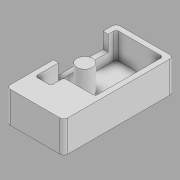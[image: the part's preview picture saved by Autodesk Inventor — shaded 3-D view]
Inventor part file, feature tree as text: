
AUTODESK INVENTOR PART (.ipt)
format: ipt  version: 2020 (Build 240168000, 168)  size: 165,376 bytes
history: native  units: in
note: dims shown in document units (in); Inventor stores cm internally (conversion verified against a paired STEP export)
features: sketch x5, extrude x4, other x1
ambient origin geometry x8: Origin, YZ Plane, XZ Plane, XY Plane, X Axis, Y Axis, Z Axis, Center Point
bodies: Body1 (feature_tree)
feature tree (10):
  other  "Sólido1"
  extrude  "Extrusión1"  Depth=4.875in
  extrude  "Extrusión2"  Depth=0.375in
  extrude  "Extrusión3"  Depth=0.375in
  extrude  "Extrusión5"  Depth=5.25in
  sketch  "Boceto7"  dims[d8=1.5in d9=0.0in d20=0.25in d21=0.25in d22=0.25in d23=1.75in d24=0.625in d25=1.5in d26=0.125in d27=1.25in d28=0.0in d29=0.625in d30=0.75in d31=2.375in d32=0.125in d33=0.25in d34=0.0in d44=0.75in d45=2.375in d46=0.875in d47=1.5in d48=0.0in]
  sketch  "Boceto1"  dims[d0=2.375in d1=4.875in]
  sketch  "Boceto3"  dims[d2=0.375in d3=0.375in]
  sketch  "Boceto4"  dims[d4=0.375in d5=0.375in]
  sketch  "Boceto6"  dims[d6=2.75in d7=5.25in]
